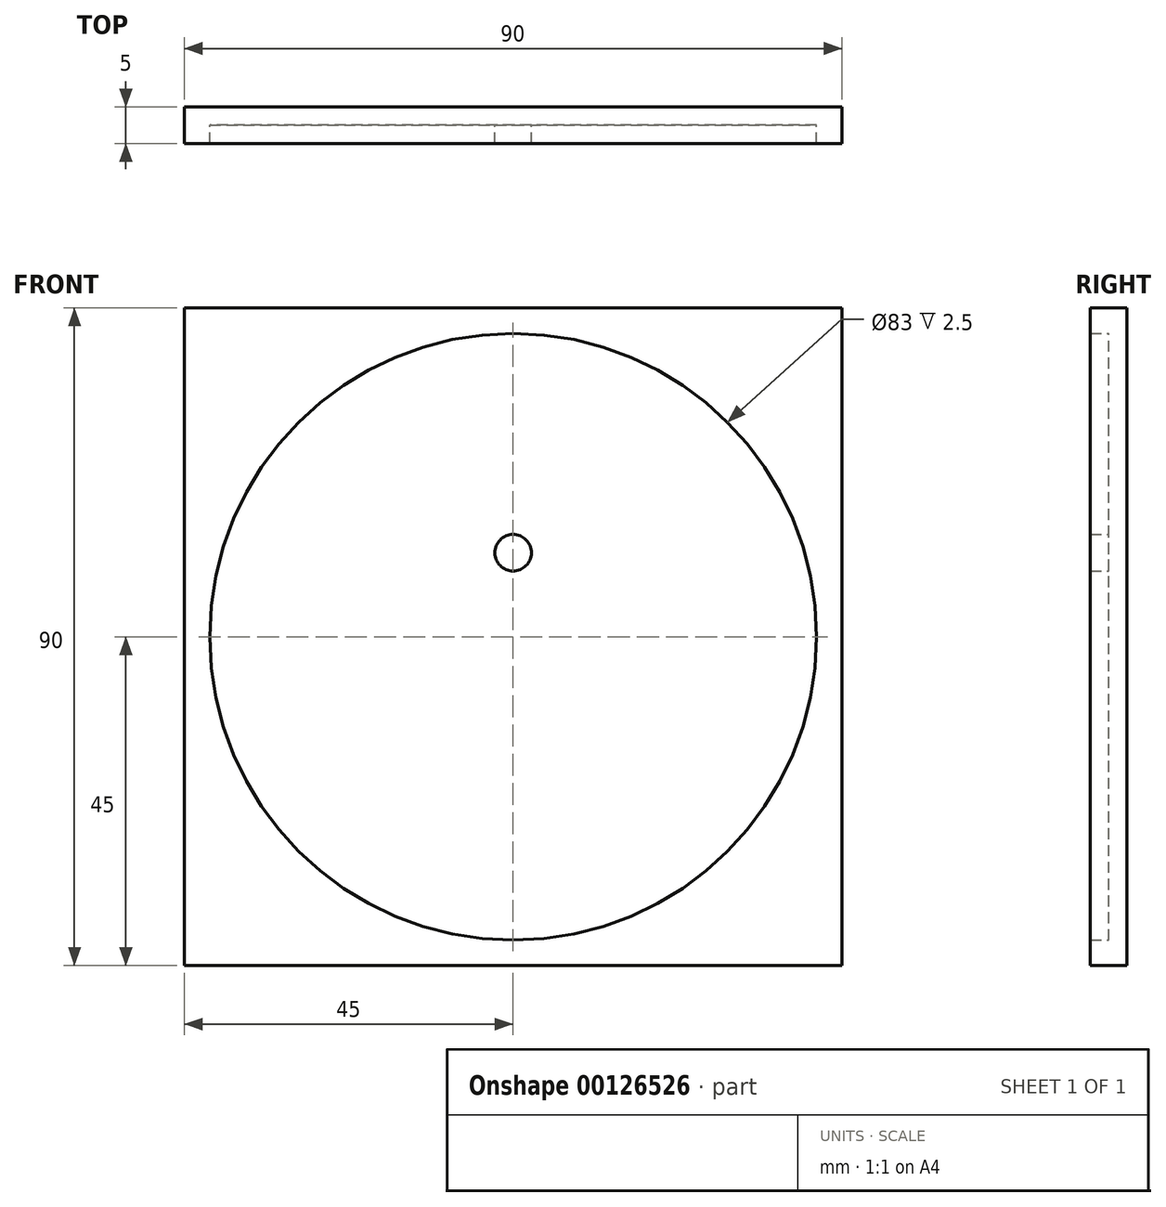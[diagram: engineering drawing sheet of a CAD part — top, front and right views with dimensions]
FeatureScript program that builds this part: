
annotation { "Feature Type Name" : "Feature", "Feature Type Description" : "" }
export const myFeature = defineFeature(function(context is Context, id is Id, definition is map)
    precondition{}
    {
        {
            var Q0;
            Q0=qCreatedBy(makeId("Front.planeOp"),FACE);
            var sketch = newSketch(context, id + "F0", { "sketchPlane" : qUnion([Q0])});
            skLineSegment(sketch, "E0.rect.bottom", {"start": v(45, -45) * mm, "end": v(-45, -45) * mm});
            skLineSegment(sketch, "E0.rect.top", {"start": v(45, 45) * mm, "end": v(-45, 45) * mm});
            skLineSegment(sketch, "E0.rect.left", {"start": v(45, -45) * mm, "end": v(45, 45) * mm});
            skLineSegment(sketch, "E0.rect.right", {"start": v(-45, -45) * mm, "end": v(-45, 45) * mm});
            skPoint(sketch, "E0.rect.middle", {"position": v(0, 0) * mm});
            skSolve(sketch);
        }
        {
            var Q0;
            Q0=qSketchRegion(id+"F0",true);
            extrude(context, id + "F1", {"entities" : qUnion([Q0]), "depth" : 2.5 * mm});
        }
        {
            var Q0;
            Q0=makeQuery(id+"F1.opExtrude","CAP_FACE",FACE,{"disambiguationData":[OSD([sQuery(id+"F0.wireOp",EDGE,"E0.rect.bottom"),sQuery(id+"F0.wireOp",EDGE,"E0.rect.top"),sQuery(id+"F0.wireOp",EDGE,"E0.rect.left"),sQuery(id+"F0.wireOp",EDGE,"E0.rect.right")])],"isStart":false});
            var sketch = newSketch(context, id + "F2", { "sketchPlane" : qUnion([Q0])});
            skCircle(sketch, "E1", {"center": v(0, 0) * mm, "radius": 41.5 * mm});
            skLineSegment(sketch, "E2.0", {"start": v(45, 45) * mm, "end": v(-45, 45) * mm});
            skLineSegment(sketch, "E2.1", {"start": v(-45, -45) * mm, "end": v(-45, 45) * mm});
            skLineSegment(sketch, "E2.2", {"start": v(45, -45) * mm, "end": v(-45, -45) * mm});
            skLineSegment(sketch, "E2.3", {"start": v(45, -45) * mm, "end": v(45, 45) * mm});
            skSolve(sketch);
        }
        {
            var Q0;
            Q0=qSketchRegion(id+"F2",true);
            extrude(context, id + "F3", {"entities" : qUnion([Q0]), "operationType" : NewBodyOperationType.ADD, "depth" : 2.5 * mm});
        }
        {
            var Q0;
            Q0=makeQuery(id+"F1.opExtrude","CAP_FACE",FACE,{"disambiguationData":[OSD([sQuery(id+"F0.wireOp",EDGE,"E0.rect.bottom"),sQuery(id+"F0.wireOp",EDGE,"E0.rect.top"),sQuery(id+"F0.wireOp",EDGE,"E0.rect.left"),sQuery(id+"F0.wireOp",EDGE,"E0.rect.right")])],"isStart":false});
            var sketch = newSketch(context, id + "F4", { "sketchPlane" : qUnion([Q0])});
            skCircle(sketch, "E3", {"center": v(0, 11.5) * mm, "radius": 2.5 * mm});
            skSolve(sketch);
        }
        {
            var Q0;
            Q0=qSketchRegion(id+"F4",true);
            extrude(context, id + "F5", {"entities" : qUnion([Q0]), "operationType" : NewBodyOperationType.ADD, "depth" : 2.5 * mm});
        }
    });
